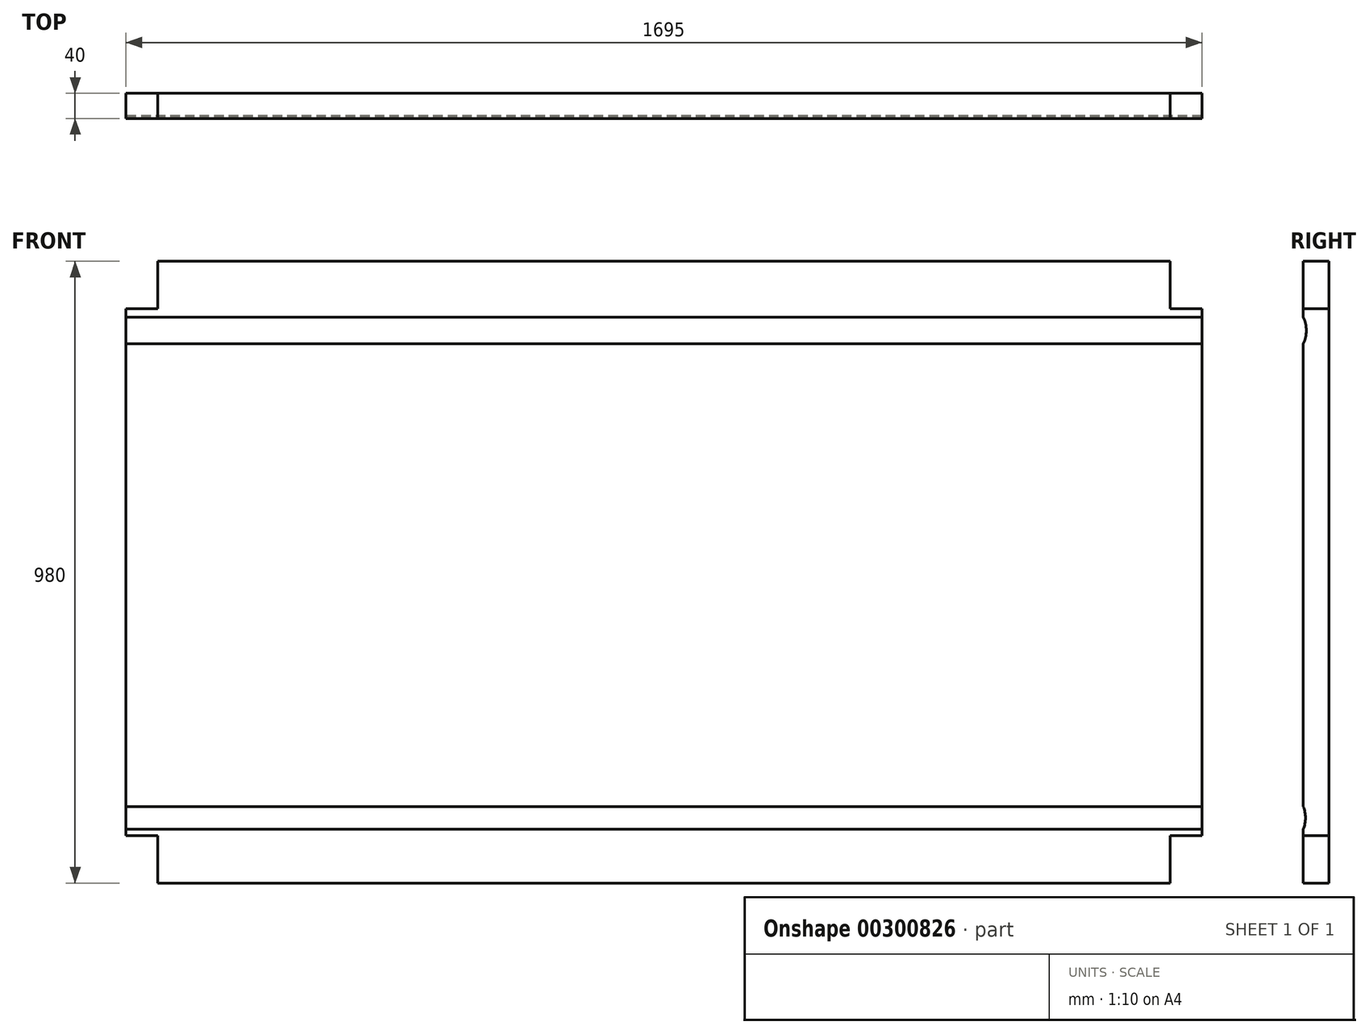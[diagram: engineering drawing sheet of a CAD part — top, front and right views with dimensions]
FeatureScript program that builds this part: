
annotation { "Feature Type Name" : "Feature", "Feature Type Description" : "" }
export const myFeature = defineFeature(function(context is Context, id is Id, definition is map)
    precondition{}
    {
        {
            var Q0;
            Q0=qCreatedBy(makeId("Front.planeOp"),FACE);
            var sketch = newSketch(context, id + "F0", { "sketchPlane" : qUnion([Q0])});
            skLineSegment(sketch, "E0.bottom", {"start": v(0, 0) * mm, "end": v(1695, 0) * mm});
            skLineSegment(sketch, "E0.top", {"start": v(0, -980) * mm, "end": v(1695, -980) * mm});
            skLineSegment(sketch, "E0.left", {"start": v(0, 0) * mm, "end": v(0, -980) * mm});
            skLineSegment(sketch, "E0.right", {"start": v(1695, 0) * mm, "end": v(1695, -980) * mm});
            skPoint(sketch, "E1.visualSharp", {"position": v(1551.45, -62.15) * mm});
            skSolve(sketch);
        }
        {
            var Q0;
            Q0=makeQuery(id+"F0.imprint","IMPRINT",FACE,{"disambiguationData":[TD([[makeQuery(id+"F0.imprint","IMPRINT",EDGE,{"derivedFrom":sQuery(id+"F0.wireOp",EDGE,"E0.bottom")}),-1.0]])]});
            extrude(context, id + "F1", {"entities" : qUnion([Q0]), "depth" : 40 * mm});
        }
        {
            var Q0;
            Q0=makeQuery(id+"F1.opExtrude","SWEPT_FACE",FACE,{"disambiguationData":[OSD([sQuery(id+"F0.wireOp",EDGE,"E0.left")])]});
            var sketch = newSketch(context, id + "F2", { "sketchPlane" : qUnion([Q0])});
            skCircle(sketch, "E2", {"center": v(85.36, -109.13) * mm, "radius": 50 * mm});
            skCircle(sketch, "E3", {"center": v(86.77, -877.35) * mm, "radius": 50 * mm});
            skSolve(sketch);
        }
        {
            var Q0;
            Q0 = qSketchRegion(id + "F2", true);
            extrude(context, id + "F3", {"entities" : qUnion([Q0]), "operationType" : NewBodyOperationType.REMOVE, "endBound" : BoundingType.THROUGH_ALL, "oppositeDirection" : true, "depth" : 25 * mm});
        }
        {
            var Q0;
            Q0=makeQuery(id+"F1.opExtrude","SWEPT_FACE",FACE,{"disambiguationData":[OSD([sQuery(id+"F0.wireOp",EDGE,"E0.bottom")])]});
            var sketch = newSketch(context, id + "F4", { "sketchPlane" : qUnion([Q0])});
            skCircle(sketch, "E4", {"center": v(140.8, -82.49) * mm, "radius": 50 * mm});
            skCircle(sketch, "E5", {"center": v(1551.46, -85.07) * mm, "radius": 50 * mm});
            skSolve(sketch);
        }
        {
            var Q0;
            {var subQ0=sQuery(id+"F4.wireOp",EDGE,"E4");var subQ1=makeQuery(id+"F1.opExtrude","CAP_EDGE",EDGE,{"disambiguationData":[OSD([sQuery(id+"F0.wireOp",EDGE,"E0.bottom")])],"isStart":false});var subQ2=makeQuery(id+"F4.imprint","INTERSECT",VERTEX,{"disambiguationData":[OD(0.0)],"derivedFrom":[subQ1,subQ0]});Q0=makeQuery(id+"F4.imprint","IMPRINT",FACE,{"disambiguationData":[TD([[makeQuery(id+"F4.imprint","IMPRINT",EDGE,{"disambiguationData":[TD([[subQ2,-1.0]])],"derivedFrom":subQ0}),1.0]])]});}
            var Q1;
            {var subQ0=sQuery(id+"F4.wireOp",EDGE,"E5");var subQ1=makeQuery(id+"F1.opExtrude","CAP_EDGE",EDGE,{"disambiguationData":[OSD([sQuery(id+"F0.wireOp",EDGE,"E0.bottom")])],"isStart":false});var subQ2=makeQuery(id+"F4.imprint","INTERSECT",VERTEX,{"disambiguationData":[OD(0.0)],"derivedFrom":[subQ1,subQ0]});Q1=makeQuery(id+"F4.imprint","IMPRINT",FACE,{"disambiguationData":[TD([[makeQuery(id+"F4.imprint","IMPRINT",EDGE,{"disambiguationData":[TD([[subQ2,1.0]])],"derivedFrom":subQ0}),1.0]])]});}
            extrude(context, id + "F5", {"entities" : qUnion([Q0, Q1]), "operationType" : NewBodyOperationType.REMOVE, "endBound" : BoundingType.THROUGH_ALL, "oppositeDirection" : true, "depth" : 850 * mm});
        }
        {
            var Q0;
            Q0=makeQuery(id+"F1.opExtrude","SWEPT_FACE",FACE,{"disambiguationData":[OSD([sQuery(id+"F0.wireOp",EDGE,"E0.left")])]});
            var sketch = newSketch(context, id + "F6", { "sketchPlane" : qUnion([Q0])});
            skLineSegment(sketch, "E6", {"start": v(0, 0) * mm, "end": v(40, 0) * mm});
            skLineSegment(sketch, "E7", {"start": v(40, 0) * mm, "end": v(40, -75) * mm});
            skLineSegment(sketch, "E8", {"start": v(40, -75) * mm, "end": v(0, -75) * mm});
            skLineSegment(sketch, "E9", {"start": v(0, -75) * mm, "end": v(0, 0) * mm});
            skLineSegment(sketch, "E10", {"start": v(40, -980) * mm, "end": v(0, -980) * mm});
            skLineSegment(sketch, "E11", {"start": v(0, -980) * mm, "end": v(0, -905) * mm});
            skLineSegment(sketch, "E12", {"start": v(0, -905) * mm, "end": v(40, -905) * mm});
            skLineSegment(sketch, "E13", {"start": v(40, -905) * mm, "end": v(40, -980) * mm});
            skSolve(sketch);
        }
        {
            var Q0;
            Q0=makeQuery(id+"F6.imprint","IMPRINT",FACE,{"disambiguationData":[TD([[makeQuery(id+"F6.imprint","IMPRINT",EDGE,{"derivedFrom":sQuery(id+"F6.wireOp",EDGE,"E6")}),1.0]])]});
            var Q1;
            Q1=makeQuery(id+"F6.imprint","IMPRINT",FACE,{"disambiguationData":[TD([[makeQuery(id+"F6.imprint","IMPRINT",EDGE,{"derivedFrom":sQuery(id+"F6.wireOp",EDGE,"E10")}),-1.0]])]});
            extrude(context, id + "F7", {"entities" : qUnion([Q0, Q1]), "operationType" : NewBodyOperationType.REMOVE, "oppositeDirection" : true, "depth" : 50 * mm});
        }
        {
            var Q0;
            Q0=makeQuery(id+"F1.opExtrude","SWEPT_FACE",FACE,{"disambiguationData":[OSD([sQuery(id+"F0.wireOp",EDGE,"E0.right")])]});
            var sketch = newSketch(context, id + "F8", { "sketchPlane" : qUnion([Q0])});
            skLineSegment(sketch, "E14", {"start": v(-40, 0) * mm, "end": v(0, 0) * mm});
            skLineSegment(sketch, "E15", {"start": v(0, 0) * mm, "end": v(0, -75) * mm});
            skLineSegment(sketch, "E16", {"start": v(0, -75) * mm, "end": v(-40, -75) * mm});
            skLineSegment(sketch, "E17", {"start": v(-40, -75) * mm, "end": v(-40, 0) * mm});
            skLineSegment(sketch, "E18", {"start": v(0, -980) * mm, "end": v(-40, -980) * mm});
            skLineSegment(sketch, "E19", {"start": v(-40, -980) * mm, "end": v(-40, -905) * mm});
            skLineSegment(sketch, "E20", {"start": v(-40, -905) * mm, "end": v(0, -905) * mm});
            skLineSegment(sketch, "E21", {"start": v(0, -905) * mm, "end": v(0, -980) * mm});
            skSolve(sketch);
        }
        {
            var Q0;
            Q0=makeQuery(id+"F8.imprint","IMPRINT",FACE,{"disambiguationData":[TD([[makeQuery(id+"F8.imprint","IMPRINT",EDGE,{"derivedFrom":sQuery(id+"F8.wireOp",EDGE,"E14")}),-1.0]])]});
            var Q1;
            Q1=makeQuery(id+"F8.imprint","IMPRINT",FACE,{"disambiguationData":[TD([[makeQuery(id+"F8.imprint","IMPRINT",EDGE,{"derivedFrom":sQuery(id+"F8.wireOp",EDGE,"E18")}),1.0]])]});
            extrude(context, id + "F9", {"entities" : qUnion([Q0, Q1]), "operationType" : NewBodyOperationType.REMOVE, "oppositeDirection" : true, "depth" : 50 * mm});
        }
    });
